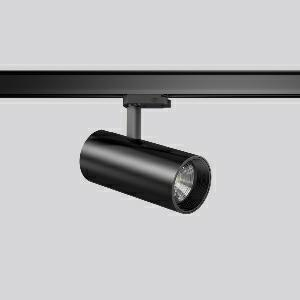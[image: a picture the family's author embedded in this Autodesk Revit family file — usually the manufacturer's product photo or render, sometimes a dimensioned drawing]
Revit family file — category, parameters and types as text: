
# Revit family: deecos_s_mini_742208_003_2_76_bc8b
name_source: partatom
category: Lighting Fixtures
units: mm (PartAtom-declared; Revit-internal decimal feet)

## family parameters
Cut with Voids When Loaded = No
Host = Face
Light Source = No
Part Type = Normal
Room Calculation Point = No
Round Connector Dimension = Use Diameter
Shared = No

## types (1)
- DEECOS S mini (1 x LED Modul 927, 2700 lm, 2700)
    Apparent Load = 29 VA
    Approval mark = CE
    CIE Flux Codes = 98 100 100 100 100
    Color Rendering = 92
    Color Temperature = 2700
    Default Elevation = 1800 mm
    Description = Series: DEECOS S mini
LED surface-mounted projector in modern design with no visible cooling ribs. Housing: die-cast aluminium, powder-coated. Rotation range: 356°. Swivel range: 90°. Black plastic ring and recessed LED to prevent glare from the side. Optical assembly with lens made of plastic (polycarbonate) for the best homogeneous light distribution - can be changed without tools. Best colour rendering index Ra>90. With adapter for RZB 3-circuit DALI tracks. Suitable for Track on ceiling, Wall track. High quality converter without flickering and stroboscopic effect. The following accessories can be mounted without use of tools: interchangeable lenses, decorative glasses, honeycomb louvre, clear and frosted diffusers, white interchangeable plastic ring. 
Colour: deep black, matt (RAL 9005)
Diameter: 87 mm
Height: 214 mm
Lamp: LED
Socket: without socket
Colour temperature: 2700K
Colour rendering index (CRI): 92
System power: 29 W
Rated luminous flux: 2700 lm
Luminous efficiency: 93 lm/W
Control gear: Converter, dimmable, DALI
Protection class: I
Type of protection: IP 20
    Height = 214 mm
    Lamp = 1 x LED Modul 927
    Lamp Light Flux = 2700 lm
    Lamp count = 1
    Length = 87 mm
    Lifetime = 50000 h
    Luminous efficacy = 93 lm/W
    Manufacturer = RZB
    ModVariant = No
    Model = 742208.003.2.76
    Mounting Place = Ceiling
    Mounting Type = Rail mounted
    Number of Poles = 1
    OnlyDefault = Yes
    Power Factor = 1
    Product Name = DEECOS S mini
    Product group = Track mounted projectors
    ProductGroupID = 301
    Protection Class = Protection class I
    Protection Degree = IP 20
    RLX_Detail_Level = 1
    RLX_Emergency_Light_Flux = 0 lm
    RLX_Emergency_Type = 0
    RLX_Emergency_Type_DB = No
    RlxData = <blob elided: 38833 chars, md5=582f63de>
    Socket = socket
    Standby Power = 0 W
    System Light Flux = 2700 lm
    System Power = 29 W
    Type Comments = Product without accessories
    Type Image = 741930.003.jpg
    URL = http://relux.com
    VarID = ---
    Voltage = 230 V
    Voltage Range = 220-240 V
    Weight = 0.00 kg
    Width = 0 mm  [stored 0 ft]

note: [stored X ft] marks values corroborated as IEEE doubles in the binary element streams (Revit-internal decimal feet)

## geometry (parser evidence)
native form markers: Blend x4, Sweep x12
no freeform markers — native parametric forms only
